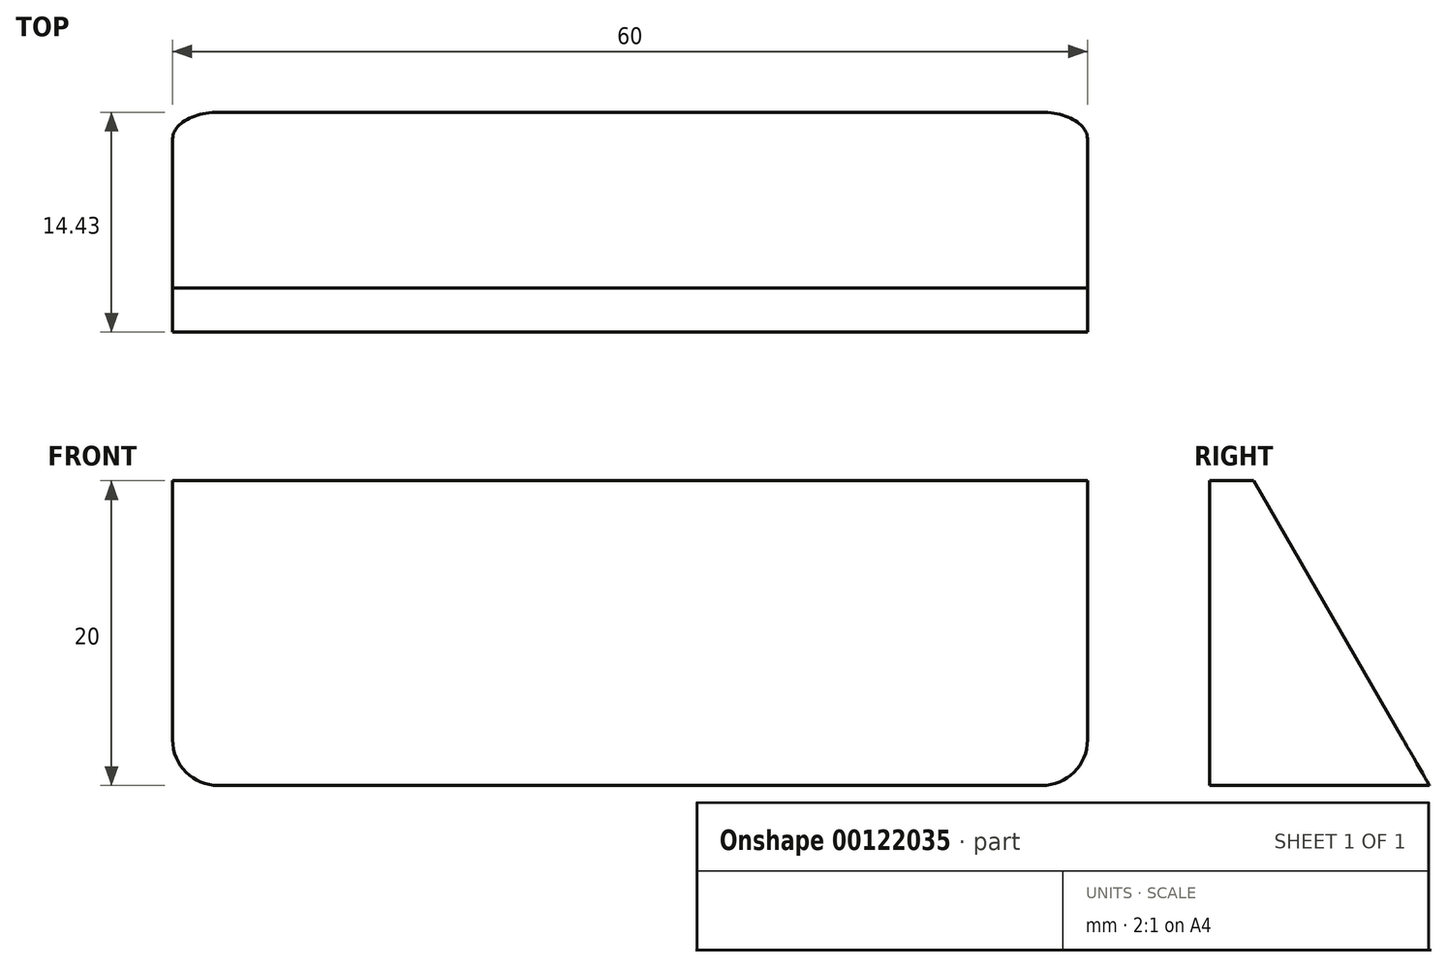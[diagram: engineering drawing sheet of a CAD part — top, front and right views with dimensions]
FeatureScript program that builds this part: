
annotation { "Feature Type Name" : "Feature", "Feature Type Description" : "" }
export const myFeature = defineFeature(function(context is Context, id is Id, definition is map)
    precondition{}
    {
        {
            var Q0;
            Q0=qCreatedBy(makeId("Front.planeOp"),FACE);
            var sketch = newSketch(context, id + "F0", { "sketchPlane" : qUnion([Q0])});
            skLineSegment(sketch, "E0.bottom", {"start": v(-30, 12.5) * mm, "end": v(30, 12.5) * mm});
            skLineSegment(sketch, "E0.top", {"start": v(-30, -12.5) * mm, "end": v(30, -12.5) * mm});
            skLineSegment(sketch, "E0.left", {"start": v(-30, 12.5) * mm, "end": v(-30, -12.5) * mm});
            skLineSegment(sketch, "E0.right", {"start": v(30, 12.5) * mm, "end": v(30, -12.5) * mm});
            skPoint(sketch, "E0.middle", {"position": v(0, 0) * mm});
            skSolve(sketch);
        }
        {
            var Q0;
            Q0=qSketchRegion(id+"F0",true);
            var Q1;
            Q1=makeQuery(id+"F0.imprint","IMPRINT",FACE,{"disambiguationData":[TD([[makeQuery(id+"F0.imprint","IMPRINT",EDGE,{"derivedFrom":sQuery(id+"F0.wireOp",EDGE,"E0.bottom")}),-1.0]])]});
            extrude(context, id + "F1", {"entities" : qUnion([Q0, Q1]), "depth" : 18 * mm});
        }
        {
            var Q0;
            Q0=qCreatedBy(makeId("Right.planeOp"),FACE);
            var sketch = newSketch(context, id + "F2", { "sketchPlane" : qUnion([Q0])});
            skPoint(sketch, "E1", {"position": v(-14.43, 0) * mm});
            skLineSegment(sketch, "E2", {"start": v(-14.43, 12.5) * mm, "end": v(-14.43, -12.5) * mm});
            skLineSegment(sketch, "E3", {"start": v(-14.43, 12.5) * mm, "end": v(0, -12.5) * mm});
            skLineSegment(sketch, "E4", {"start": v(0, 0) * mm, "end": v(0, -19) * mm});
            skLineSegment(sketch, "E5", {"start": v(-14.43, 12.5) * mm, "end": v(0, 12.5) * mm});
            skLineSegment(sketch, "E6", {"start": v(0, 12.5) * mm, "end": v(0, -12.5) * mm});
            skLineSegment(sketch, "E7.bottom", {"start": v(-17.32, 12.5) * mm, "end": v(-19.79, 12.5) * mm});
            skLineSegment(sketch, "E7.top", {"start": v(-17.32, -12.5) * mm, "end": v(-19.79, -12.5) * mm});
            skLineSegment(sketch, "E7.right", {"start": v(-19.79, 12.5) * mm, "end": v(-19.79, -12.5) * mm});
            skLineSegment(sketch, "E8", {"start": v(-14.43, 7.5) * mm, "end": v(-11.55, 7.5) * mm});
            skLineSegment(sketch, "E9", {"start": v(-17.32, 12.5) * mm, "end": v(-14.43, 12.5) * mm});
            skLineSegment(sketch, "E10", {"start": v(-17.32, -12.5) * mm, "end": v(-14.43, -12.5) * mm});
            skSolve(sketch);
        }
        {
            var Q0;
            {var subQ5=sQuery(id+"F2.wireOp",EDGE,"E5");Q0=makeQuery(id+"F2.imprint","IMPRINT",FACE,{"disambiguationData":[TD([[makeQuery(id+"F2.imprint","IMPRINT",EDGE,{"derivedFrom":subQ5}),-1.0]])]});}
            var Q1;
            {var subQ0=sQuery(id+"F2.wireOp",EDGE,"E6");var subQ1=sQuery(id+"F2.wireOp",EDGE,"58584ab8-a6b6-4922-906c-b0adb40993d0");var subQ2=makeQuery(id+"F2.imprint","INTERSECT",VERTEX,{"derivedFrom":[subQ1,subQ0]});Q1=makeQuery(id+"F2.imprint","IMPRINT",FACE,{"disambiguationData":[TD([[makeQuery(id+"F2.imprint","IMPRINT",EDGE,{"disambiguationData":[TD([[subQ2,-1.0]])],"derivedFrom":subQ1}),1.0]])]});}
            var Q2;
            {var subQ3=sQuery(id+"F2.wireOp",EDGE,"E7.bottom");Q2=makeQuery(id+"F2.imprint","IMPRINT",FACE,{"disambiguationData":[TD([[makeQuery(id+"F2.imprint","IMPRINT",EDGE,{"derivedFrom":subQ3}),1.0]])]});}
            var Q3;
            {var subQ2=sQuery(id+"F2.wireOp",EDGE,"e18aa89c-91a1-443c-a1b0-1418db82612f");Q3=makeQuery(id+"F2.imprint","IMPRINT",FACE,{"disambiguationData":[TD([[makeQuery(id+"F2.imprint","IMPRINT",EDGE,{"derivedFrom":subQ2}),1.0]])]});}
            var Q4;
            {var subQ3=sQuery(id+"F2.wireOp",EDGE,"E8");Q4=makeQuery(id+"F2.imprint","IMPRINT",FACE,{"disambiguationData":[TD([[makeQuery(id+"F2.imprint","IMPRINT",EDGE,{"derivedFrom":subQ3}),1.0]])]});}
            extrude(context, id + "F3", {"entities" : qUnion([Q0, Q1, Q2, Q3, Q4]), "operationType" : NewBodyOperationType.REMOVE, "endBound" : BoundingType.SYMMETRIC, "depth" : 60 * mm});
        }
        {
            var Q0;
            Q0=makeQuery(id+"F1.opExtrude","SWEPT_EDGE",EDGE,{"disambiguationData":[OSD([sQuery(id+"F0.wireOp",EDGE,"E0.top"),sQuery(id+"F0.wireOp",EDGE,"E0.right")])]});
            var Q1;
            Q1=makeQuery(id+"F1.opExtrude","SWEPT_EDGE",EDGE,{"disambiguationData":[OSD([sQuery(id+"F0.wireOp",EDGE,"E0.top"),sQuery(id+"F0.wireOp",EDGE,"E0.left")])]});
            var Q2;
            Q2=makeQuery(id+"F3.boolean.opBoolean","COPY",EDGE,{"derivedFrom":makeQuery(id+"F3.opExtrude","SWEPT_EDGE",EDGE,{"disambiguationData":[OSD([sQuery(id+"F2.wireOp",EDGE,"E7.top"),sQuery(id+"F2.wireOp",EDGE,"E7.left")])]})});
            var Q3;
            Q3=makeQuery(id+"F3.boolean.opBoolean","COPY",EDGE,{"derivedFrom":makeQuery(id+"F3.opExtrude","CAP_EDGE",EDGE,{"disambiguationData":[OSD([sQuery(id+"F2.wireOp",EDGE,"E7.left")])],"isStart":false})});
            var Q4;
            Q4=makeQuery(id+"F3.boolean.opBoolean","COPY",EDGE,{"derivedFrom":makeQuery(id+"F3.opExtrude","CAP_EDGE",EDGE,{"disambiguationData":[OSD([sQuery(id+"F2.wireOp",EDGE,"E7.left")])],"isStart":true})});
            var Q5;
            Q5=makeQuery(id+"F3.boolean.opBoolean","COPY",EDGE,{"derivedFrom":makeQuery(id+"F3.opExtrude","SWEPT_EDGE",EDGE,{"disambiguationData":[OSD([sQuery(id+"F2.wireOp",EDGE,"E2"),sQuery(id+"F2.wireOp",EDGE,"E10")])]})});
            var Q6;
            Q6=makeQuery(id+"F3.boolean.opBoolean","COPY",EDGE,{"derivedFrom":makeQuery(id+"F3.opExtrude","CAP_EDGE",EDGE,{"disambiguationData":[OSD([sQuery(id+"F2.wireOp",EDGE,"E2")])],"isStart":false})});
            var Q7;
            Q7=makeQuery(id+"F3.boolean.opBoolean","COPY",EDGE,{"derivedFrom":makeQuery(id+"F3.opExtrude","CAP_EDGE",EDGE,{"disambiguationData":[OSD([sQuery(id+"F2.wireOp",EDGE,"E2")])],"isStart":true})});
            fillet(context, id + "F4", {"entities" : qUnion([Q0, Q1, Q2, Q3, Q4, Q5, Q6, Q7]), "radius" : 3 * mm, "tangentPropagation" : true, "allowEdgeOverflow" : false});
        }
    });
